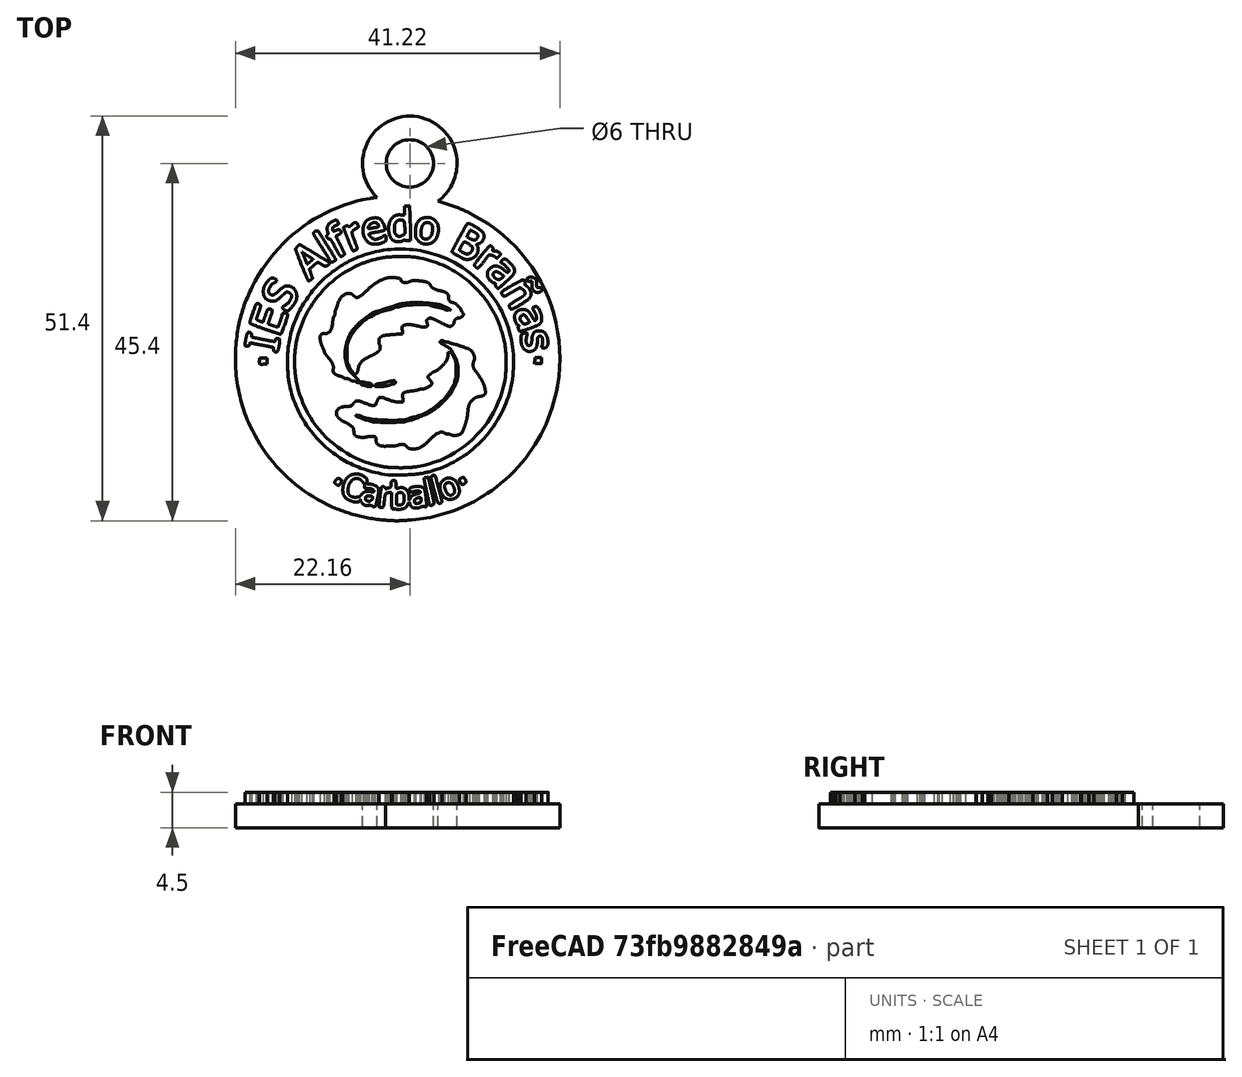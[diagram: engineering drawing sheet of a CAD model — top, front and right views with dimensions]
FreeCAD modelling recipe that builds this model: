
FCSTD DOCUMENT  (FreeCAD 0.18R16093 +53 (Git))
Label: Chaveiro_IES_AlfredoBranas
License: All rights reserved
LicenseURL: http://en.wikipedia.org/wiki/All_rights_reserved
objects: Part::Feature×90, Part::Extrusion×49, Part::Cut×15, Part::MultiFuse×3, Part::Cylinder×2
note: 159 computed .brp shape members not serialized (recipe doc carries the construction recipe); baked Part::Feature solids carry a one-line shape summary decoded from their .brp

FEATURE [Part::Feature] path55
  shape: bbox 42.61 x 41.74 x 2e-07 mm, 1 faces, 0 solids (baked)
FEATURE [Part::Feature] path55002
  shape: bbox 6.061 x 3.668 x 2e-07 mm, 1 faces, 0 solids (baked)
FEATURE [Part::Feature] path55003
  shape: bbox 3.579 x 3.321 x 2e-07 mm, 1 faces, 0 solids (baked)
FEATURE [Part::Feature] path55004
  shape: bbox 1.385 x 2.117 x 2e-07 mm, 1 faces, 0 solids (baked)
FEATURE [Part::Feature] path55005
  shape: bbox 1.072 x 1.725 x 2e-07 mm, 1 faces, 0 solids (baked)
FEATURE [Part::Feature] path55006
  shape: bbox 1.986 x 2.775 x 2e-07 mm, 1 faces, 0 solids (baked)
FEATURE [Part::Feature] path55007
  shape: bbox 1.276 x 1.287 x 2e-07 mm, 1 faces, 0 solids (baked)
FEATURE [Part::Feature] path55008
  shape: bbox 0.8533 x 0.8673 x 2e-07 mm, 1 faces, 0 solids (baked)
FEATURE [Part::Feature] path55009
  shape: bbox 4.663 x 4.271 x 2e-07 mm, 1 faces, 0 solids (baked)
FEATURE [Part::Feature] path55010
  shape: bbox 2.231 x 2.679 x 2e-07 mm, 1 faces, 0 solids (baked)
FEATURE [Part::Feature] path55011
  shape: bbox 1.459 x 1.242 x 2e-07 mm, 1 faces, 0 solids (baked)
FEATURE [Part::Feature] path55012
  shape: bbox 1.04 x 0.7778 x 2e-07 mm, 1 faces, 0 solids (baked)
FEATURE [Part::Feature] path55013
  shape: bbox 3.128 x 3.518 x 2e-07 mm, 1 faces, 0 solids (baked)
FEATURE [Part::Feature] path55014
  shape: bbox 3.478 x 2.454 x 2e-07 mm, 1 faces, 0 solids (baked)
FEATURE [Part::Feature] path55015
  shape: bbox 1.292 x 3.612 x 2e-07 mm, 1 faces, 0 solids (baked)
FEATURE [Part::Feature] path55016
  shape: bbox 0.9434 x 3.157 x 2e-07 mm, 1 faces, 0 solids (baked)
FEATURE [Part::Feature] path55017
  shape: bbox 1.497 x 3.752 x 2e-07 mm, 1 faces, 0 solids (baked)
FEATURE [Part::Feature] path55018
  shape: bbox 1.034 x 3.318 x 2e-07 mm, 1 faces, 0 solids (baked)
FEATURE [Part::Feature] path55019
  shape: bbox 2.911 x 2.992 x 2e-07 mm, 1 faces, 0 solids (baked)
FEATURE [Part::Feature] path55020
  shape: bbox 2.421 x 2.668 x 2e-07 mm, 1 faces, 0 solids (baked)
FEATURE [Part::Feature] path55021
  shape: bbox 1.627 x 2.283 x 2e-07 mm, 1 faces, 0 solids (baked)
FEATURE [Part::Feature] path55022
  shape: bbox 1.515 x 1.829 x 2e-07 mm, 1 faces, 0 solids (baked)
FEATURE [Part::Feature] path55023
  shape: bbox 0.9527 x 1.028 x 2e-07 mm, 1 faces, 0 solids (baked)
FEATURE [Part::Feature] path55024
  shape: bbox 0.4535 x 0.6054 x 2e-07 mm, 1 faces, 0 solids (baked)
FEATURE [Part::Feature] path55025
  shape: bbox 0.9424 x 1.049 x 2e-07 mm, 1 faces, 0 solids (baked)
FEATURE [Part::Feature] path55026
  shape: bbox 0.4617 x 0.5401 x 2e-07 mm, 1 faces, 0 solids (baked)
FEATURE [Part::Feature] path55027
  shape: bbox 29.22 x 29.06 x 2e-07 mm, 1 faces, 0 solids (baked)
FEATURE [Part::Feature] path55028
  shape: bbox 29.61 x 29.75 x 2e-07 mm, 1 faces, 0 solids (baked)
FEATURE [Part::Feature] path55029
  shape: bbox 27.42 x 27.59 x 2e-07 mm, 1 faces, 0 solids (baked)
FEATURE [Part::Feature] path55030
  shape: bbox 27.03 x 26.91 x 2e-07 mm, 1 faces, 0 solids (baked)
FEATURE [Part::Feature] path55031
  shape: bbox 18.97 x 13.82 x 2e-07 mm, 1 faces, 0 solids (baked)
FEATURE [Part::Feature] path55032
  shape: bbox 18.57 x 13.17 x 2e-07 mm, 1 faces, 0 solids (baked)
FEATURE [Part::Feature] path55033
  shape: bbox 1.628 x 0.6369 x 2e-07 mm, 1 faces, 0 solids (baked)
FEATURE [Part::Feature] path55034
  shape: bbox 2.68 x 0.7825 x 2e-07 mm, 1 faces, 0 solids (baked)
FEATURE [Part::Feature] path55035
  shape: bbox 18.3 x 13.46 x 2e-07 mm, 1 faces, 0 solids (baked)
FEATURE [Part::Feature] path55036
  shape: bbox 17.74 x 12.84 x 2e-07 mm, 1 faces, 0 solids (baked)
FEATURE [Part::Feature] path55037
  shape: bbox 0.9811 x 0.8129 x 2e-07 mm, 1 faces, 0 solids (baked)
FEATURE [Part::Feature] path55038
  shape: bbox 0.7466 x 0.567 x 2e-07 mm, 1 faces, 0 solids (baked)
FEATURE [Part::Feature] path55039
  shape: bbox 0.9057 x 0.8199 x 2e-07 mm, 1 faces, 0 solids (baked)
FEATURE [Part::Feature] path55040
  shape: bbox 0.5973 x 0.512 x 2e-07 mm, 1 faces, 0 solids (baked)
FEATURE [Part::Feature] path55041
  shape: bbox 4.394 x 2.557 x 2e-07 mm, 1 faces, 0 solids (baked)
FEATURE [Part::Feature] path55042
  shape: bbox 4.112 x 2.264 x 2e-07 mm, 1 faces, 0 solids (baked)
FEATURE [Part::Feature] path55043
  shape: bbox 3.481 x 2.717 x 2e-07 mm, 1 faces, 0 solids (baked)
FEATURE [Part::Feature] path55044
  shape: bbox 3.298 x 2.6 x 2e-07 mm, 1 faces, 0 solids (baked)
FEATURE [Part::Feature] path55045
  shape: bbox 4.911 x 3.979 x 2e-07 mm, 1 faces, 0 solids (baked)
FEATURE [Part::Feature] path55046
  shape: bbox 4.39 x 3.462 x 2e-07 mm, 1 faces, 0 solids (baked)
FEATURE [Part::Feature] path55047
  shape: bbox 3.605 x 3.157 x 2e-07 mm, 1 faces, 0 solids (baked)
FEATURE [Part::Feature] path55048
  shape: bbox 3.359 x 2.795 x 2e-07 mm, 1 faces, 0 solids (baked)
FEATURE [Part::Feature] path55049
  shape: bbox 1.712 x 1.573 x 2e-07 mm, 1 faces, 0 solids (baked)
FEATURE [Part::Feature] path55050
  shape: bbox 1.261 x 1.265 x 2e-07 mm, 1 faces, 0 solids (baked)
FEATURE [Part::Feature] path55051
  shape: bbox 4.529 x 4.348 x 2e-07 mm, 1 faces, 0 solids (baked)
FEATURE [Part::Feature] path55052
  shape: bbox 4.156 x 3.945 x 2e-07 mm, 1 faces, 0 solids (baked)
FEATURE [Part::Feature] path55053
  shape: bbox 3.991 x 3.755 x 2e-07 mm, 1 faces, 0 solids (baked)
FEATURE [Part::Feature] path55054
  shape: bbox 3.399 x 3.294 x 2e-07 mm, 1 faces, 0 solids (baked)
FEATURE [Part::Feature] path55055
  shape: bbox 2.278 x 2.07 x 2e-07 mm, 1 faces, 0 solids (baked)
FEATURE [Part::Feature] path55056
  shape: bbox 1.608 x 1.762 x 2e-07 mm, 1 faces, 0 solids (baked)
FEATURE [Part::Feature] path55057
  shape: bbox 3.883 x 3.859 x 2e-07 mm, 1 faces, 0 solids (baked)
FEATURE [Part::Feature] path55058
  shape: bbox 3.461 x 3.318 x 2e-07 mm, 1 faces, 0 solids (baked)
FEATURE [Part::Feature] path55059
  shape: bbox 1.711 x 1.509 x 2e-07 mm, 1 faces, 0 solids (baked)
FEATURE [Part::Feature] path55060
  shape: bbox 1.522 x 1.079 x 2e-07 mm, 1 faces, 0 solids (baked)
FEATURE [Part::Feature] path55061
  shape: bbox 4.369 x 4.646 x 2e-07 mm, 1 faces, 0 solids (baked)
FEATURE [Part::Feature] path55062
  shape: bbox 3.885 x 4.096 x 2e-07 mm, 1 faces, 0 solids (baked)
FEATURE [Part::Feature] path55063
  shape: bbox 1.848 x 2.086 x 2e-07 mm, 1 faces, 0 solids (baked)
FEATURE [Part::Feature] path55064
  shape: bbox 1.372 x 1.537 x 2e-07 mm, 1 faces, 0 solids (baked)
FEATURE [Part::Feature] path55065
  shape: bbox 3.325 x 2.896 x 2e-07 mm, 1 faces, 0 solids (baked)
FEATURE [Part::Feature] path55066
  shape: bbox 2.837 x 2.413 x 2e-07 mm, 1 faces, 0 solids (baked)
FEATURE [Part::Feature] path55067
  shape: bbox 2.873 x 4.076 x 2e-07 mm, 1 faces, 0 solids (baked)
FEATURE [Part::Feature] path55068
  shape: bbox 2.418 x 3.68 x 2e-07 mm, 1 faces, 0 solids (baked)
FEATURE [Part::Feature] path55069
  shape: bbox 4.187 x 4.703 x 2e-07 mm, 1 faces, 0 solids (baked)
FEATURE [Part::Feature] path55070
  shape: bbox 3.672 x 4.259 x 2e-07 mm, 1 faces, 0 solids (baked)
FEATURE [Part::Feature] path55071
  shape: bbox 2.278 x 1.964 x 2e-07 mm, 1 faces, 0 solids (baked)
FEATURE [Part::Feature] path55072
  shape: bbox 1.728 x 1.688 x 2e-07 mm, 1 faces, 0 solids (baked)
FEATURE [Part::Feature] path55073
  shape: bbox 2.013 x 1.62 x 2e-07 mm, 1 faces, 0 solids (baked)
FEATURE [Part::Feature] path55074
  shape: bbox 1.478 x 1.273 x 2e-07 mm, 1 faces, 0 solids (baked)
FEATURE [Part::Feature] path55075
  shape: bbox 2.371 x 4.711 x 2e-07 mm, 1 faces, 0 solids (baked)
FEATURE [Part::Feature] path55076
  shape: bbox 1.938 x 4.293 x 2e-07 mm, 1 faces, 0 solids (baked)
FEATURE [Part::Feature] path55077
  shape: bbox 1.959 x 3.712 x 2e-07 mm, 1 faces, 0 solids (baked)
FEATURE [Part::Feature] path55078
  shape: bbox 1.513 x 3.257 x 2e-07 mm, 1 faces, 0 solids (baked)
FEATURE [Part::Feature] path55079
  shape: bbox 3.202 x 3.458 x 2e-07 mm, 1 faces, 0 solids (baked)
FEATURE [Part::Feature] path55080
  shape: bbox 2.817 x 3.087 x 2e-07 mm, 1 faces, 0 solids (baked)
FEATURE [Part::Feature] path55081
  shape: bbox 1.855 x 1.145 x 2e-07 mm, 1 faces, 0 solids (baked)
FEATURE [Part::Feature] path55082
  shape: bbox 1.522 x 0.9057 x 2e-07 mm, 1 faces, 0 solids (baked)
FEATURE [Part::Feature] path55083
  shape: bbox 3.154 x 3.493 x 2e-07 mm, 1 faces, 0 solids (baked)
FEATURE [Part::Feature] path55084
  shape: bbox 2.742 x 3.32 x 2e-07 mm, 1 faces, 0 solids (baked)
FEATURE [Part::Feature] path55085
  shape: bbox 1.893 x 2.907 x 2e-07 mm, 1 faces, 0 solids (baked)
FEATURE [Part::Feature] path55086
  shape: bbox 1.599 x 2.338 x 2e-07 mm, 1 faces, 0 solids (baked)
FEATURE [Part::Feature] path55087
  shape: bbox 2.901 x 4.614 x 2e-07 mm, 1 faces, 0 solids (baked)
FEATURE [Part::Feature] path55088
  shape: bbox 2.574 x 4.276 x 2e-07 mm, 1 faces, 0 solids (baked)
FEATURE [Part::Feature] path55089
  shape: bbox 1.694 x 2.496 x 2e-07 mm, 1 faces, 0 solids (baked)
FEATURE [Part::Feature] path55090
  shape: bbox 1.455 x 2.377 x 2e-07 mm, 1 faces, 0 solids (baked)
FEATURE [Part::Extrusion] Extrude
  Base = -> path55002
  Dir = (0,0,1)
  DirMode = 0
  FaceMakerClass = Part::FaceMakerBullseye
  LengthFwd = 1.5
  LengthRev = 0
  Solid = true
  Symmetric = false
FEATURE [Part::Extrusion] Extrude003
  Base = -> path55005
  Dir = (0,0,1)
  DirMode = 0
  FaceMakerClass = Part::FaceMakerBullseye
  LengthFwd = 1.5
  LengthRev = 0
  Solid = true
  Symmetric = false
FEATURE [Part::Extrusion] Extrude006
  Base = -> path55008
  Dir = (0,0,1)
  DirMode = 0
  FaceMakerClass = Part::FaceMakerBullseye
  LengthFwd = 1.5
  LengthRev = 0
  Solid = true
  Symmetric = false
FEATURE [Part::Extrusion] Extrude007
  Base = -> path55009
  Dir = (0,0,1)
  DirMode = 0
  FaceMakerClass = Part::FaceMakerBullseye
  LengthFwd = 1.5
  LengthRev = 0
  Solid = true
  Symmetric = false
FEATURE [Part::Extrusion] Extrude010
  Base = -> path55012
  Dir = (0,0,1)
  DirMode = 0
  FaceMakerClass = Part::FaceMakerBullseye
  LengthFwd = 7.5
  LengthRev = 0
  Placement = pos=(0,0,-2) rot=(0,0,1;0rad)
  Solid = true
  Symmetric = false
FEATURE [Part::Extrusion] Extrude012
  Base = -> path55014
  Dir = (0,0,1)
  DirMode = 0
  FaceMakerClass = Part::FaceMakerBullseye
  LengthFwd = 1.5
  LengthRev = 0
  Solid = true
  Symmetric = false
FEATURE [Part::Extrusion] Extrude013
  Base = -> path55015
  Dir = (0,0,1)
  DirMode = 0
  FaceMakerClass = Part::FaceMakerBullseye
  LengthFwd = 1.5
  LengthRev = 0
  Solid = true
  Symmetric = false
FEATURE [Part::Extrusion] Extrude015
  Base = -> path55017
  Dir = (0,0,1)
  DirMode = 0
  FaceMakerClass = Part::FaceMakerBullseye
  LengthFwd = 1.5
  LengthRev = 0
  Solid = true
  Symmetric = false
FEATURE [Part::Extrusion] Extrude017
  Base = -> path55019
  Dir = (0,0,1)
  DirMode = 0
  FaceMakerClass = Part::FaceMakerBullseye
  LengthFwd = 1.5
  LengthRev = 0
  Solid = true
  Symmetric = false
FEATURE [Part::Extrusion] Extrude020
  Base = -> path55022
  Dir = (0,0,1)
  DirMode = 0
  FaceMakerClass = Part::FaceMakerBullseye
  LengthFwd = 1.5
  LengthRev = 0
  Solid = true
  Symmetric = false
FEATURE [Part::Extrusion] Extrude021
  Base = -> path55023
  Dir = (0,0,1)
  DirMode = 0
  FaceMakerClass = Part::FaceMakerBullseye
  LengthFwd = 1.5
  LengthRev = 0
  Solid = true
  Symmetric = false
FEATURE [Part::Extrusion] Extrude022
  Base = -> path55024
  Dir = (0,0,1)
  DirMode = 0
  FaceMakerClass = Part::FaceMakerBullseye
  LengthFwd = 1.5
  LengthRev = 0
  Solid = true
  Symmetric = false
FEATURE [Part::Extrusion] Extrude023
  Base = -> path55025
  Dir = (0,0,1)
  DirMode = 0
  FaceMakerClass = Part::FaceMakerBullseye
  LengthFwd = 1.5
  LengthRev = 0
  Solid = true
  Symmetric = false
FEATURE [Part::Extrusion] Extrude025
  Base = -> path55027
  Dir = (0,0,1)
  DirMode = 0
  FaceMakerClass = Part::FaceMakerBullseye
  LengthFwd = 1.5
  LengthRev = 0
  Solid = true
  Symmetric = false
FEATURE [Part::Extrusion] Extrude028
  Base = -> path55030
  Dir = (0,0,1)
  DirMode = 0
  FaceMakerClass = Part::FaceMakerBullseye
  LengthFwd = 1.5
  LengthRev = 0
  Solid = true
  Symmetric = false
FEATURE [Part::Extrusion] Extrude029
  Base = -> path55031
  Dir = (0,0,1)
  DirMode = 0
  FaceMakerClass = Part::FaceMakerBullseye
  LengthFwd = 1.5
  LengthRev = 0
  Solid = true
  Symmetric = false
FEATURE [Part::Extrusion] Extrude030
  Base = -> path55032
  Dir = (0,0,1)
  DirMode = 0
  FaceMakerClass = Part::FaceMakerBullseye
  LengthFwd = 1.5
  LengthRev = 0
  Solid = true
  Symmetric = false
FEATURE [Part::Extrusion] Extrude031
  Base = -> path55033
  Dir = (0,0,1)
  DirMode = 0
  FaceMakerClass = Part::FaceMakerBullseye
  LengthFwd = 1.5
  LengthRev = 0
  Solid = true
  Symmetric = false
FEATURE [Part::Extrusion] Extrude032
  Base = -> path55034
  Dir = (0,0,1)
  DirMode = 0
  FaceMakerClass = Part::FaceMakerBullseye
  LengthFwd = 1.5
  LengthRev = 0
  Solid = true
  Symmetric = false
FEATURE [Part::Extrusion] Extrude033
  Base = -> path55035
  Dir = (0,0,1)
  DirMode = 0
  FaceMakerClass = Part::FaceMakerBullseye
  LengthFwd = 1.5
  LengthRev = 0
  Solid = true
  Symmetric = false
FEATURE [Part::Extrusion] Extrude034
  Base = -> path55036
  Dir = (0,0,1)
  DirMode = 0
  FaceMakerClass = Part::FaceMakerBullseye
  LengthFwd = 1.5
  LengthRev = 0
  Solid = true
  Symmetric = false
FEATURE [Part::Extrusion] Extrude035
  Base = -> path55037
  Dir = (0,0,1)
  DirMode = 0
  FaceMakerClass = Part::FaceMakerBullseye
  LengthFwd = 1.5
  LengthRev = 0
  Solid = true
  Symmetric = false
FEATURE [Part::Extrusion] Extrude037
  Base = -> path55039
  Dir = (0,0,1)
  DirMode = 0
  FaceMakerClass = Part::FaceMakerBullseye
  LengthFwd = 1.5
  LengthRev = 0
  Solid = true
  Symmetric = false
FEATURE [Part::Extrusion] Extrude039
  Base = -> path55041
  Dir = (0,0,1)
  DirMode = 0
  FaceMakerClass = Part::FaceMakerBullseye
  LengthFwd = 1.5
  LengthRev = 0
  Solid = true
  Symmetric = false
FEATURE [Part::Extrusion] Extrude041
  Base = -> path55043
  Dir = (0,0,1)
  DirMode = 0
  FaceMakerClass = Part::FaceMakerBullseye
  LengthFwd = 1.5
  LengthRev = 0
  Solid = true
  Symmetric = false
FEATURE [Part::Extrusion] Extrude043
  Base = -> path55045
  Dir = (0,0,1)
  DirMode = 0
  FaceMakerClass = Part::FaceMakerBullseye
  LengthFwd = 1.5
  LengthRev = 0
  Solid = true
  Symmetric = false
FEATURE [Part::Extrusion] Extrude045
  Base = -> path55047
  Dir = (0,0,1)
  DirMode = 0
  FaceMakerClass = Part::FaceMakerBullseye
  LengthFwd = 1.5
  LengthRev = 0
  Solid = true
  Symmetric = false
FEATURE [Part::Extrusion] Extrude048
  Base = -> path55050
  Dir = (0,0,1)
  DirMode = 0
  FaceMakerClass = Part::FaceMakerBullseye
  LengthFwd = 1.5
  LengthRev = 0
  Solid = true
  Symmetric = false
FEATURE [Part::Extrusion] Extrude049
  Base = -> path55051
  Dir = (0,0,1)
  DirMode = 0
  FaceMakerClass = Part::FaceMakerBullseye
  LengthFwd = 1.5
  LengthRev = 0
  Solid = true
  Symmetric = false
FEATURE [Part::Extrusion] Extrude051
  Base = -> path55053
  Dir = (0,0,1)
  DirMode = 0
  FaceMakerClass = Part::FaceMakerBullseye
  LengthFwd = 1.5
  LengthRev = 0
  Solid = true
  Symmetric = false
FEATURE [Part::Extrusion] Extrude053
  Base = -> path55055
  Dir = (0,0,1)
  DirMode = 0
  FaceMakerClass = Part::FaceMakerBullseye
  LengthFwd = 1.5
  LengthRev = 0
  Solid = true
  Symmetric = false
FEATURE [Part::Extrusion] Extrude055
  Base = -> path55057
  Dir = (0,0,1)
  DirMode = 0
  FaceMakerClass = Part::FaceMakerBullseye
  LengthFwd = 1.5
  LengthRev = 0
  Solid = true
  Symmetric = false
FEATURE [Part::Extrusion] Extrude058
  Base = -> path55060
  Dir = (0,0,1)
  DirMode = 0
  FaceMakerClass = Part::FaceMakerBullseye
  LengthFwd = 1.5
  LengthRev = 0
  Solid = true
  Symmetric = false
FEATURE [Part::Extrusion] Extrude059
  Base = -> path55061
  Dir = (0,0,1)
  DirMode = 0
  FaceMakerClass = Part::FaceMakerBullseye
  LengthFwd = 1.5
  LengthRev = 0
  Solid = true
  Symmetric = false
FEATURE [Part::Extrusion] Extrude062
  Base = -> path55064
  Dir = (0,0,1)
  DirMode = 0
  FaceMakerClass = Part::FaceMakerBullseye
  LengthFwd = 1.5
  LengthRev = 0
  Solid = true
  Symmetric = false
FEATURE [Part::Extrusion] Extrude063
  Base = -> path55065
  Dir = (0,0,1)
  DirMode = 0
  FaceMakerClass = Part::FaceMakerBullseye
  LengthFwd = 1.5
  LengthRev = 0
  Solid = true
  Symmetric = false
FEATURE [Part::Extrusion] Extrude065
  Base = -> path55067
  Dir = (0,0,1)
  DirMode = 0
  FaceMakerClass = Part::FaceMakerBullseye
  LengthFwd = 1.5
  LengthRev = 0
  Solid = true
  Symmetric = false
FEATURE [Part::Extrusion] Extrude067
  Base = -> path55069
  Dir = (0,0,1)
  DirMode = 0
  FaceMakerClass = Part::FaceMakerBullseye
  LengthFwd = 1.5
  LengthRev = 0
  Solid = true
  Symmetric = false
FEATURE [Part::Extrusion] Extrude070
  Base = -> path55072
  Dir = (0,0,1)
  DirMode = 0
  FaceMakerClass = Part::FaceMakerBullseye
  LengthFwd = 1.5
  LengthRev = 0
  Solid = true
  Symmetric = false
FEATURE [Part::Extrusion] Extrude072
  Base = -> path55074
  Dir = (0,0,1)
  DirMode = 0
  FaceMakerClass = Part::FaceMakerBullseye
  LengthFwd = 1.5
  LengthRev = 0
  Solid = true
  Symmetric = false
FEATURE [Part::Extrusion] Extrude073
  Base = -> path55075
  Dir = (0,0,1)
  DirMode = 0
  FaceMakerClass = Part::FaceMakerBullseye
  LengthFwd = 1.5
  LengthRev = 0
  Solid = true
  Symmetric = false
FEATURE [Part::Extrusion] Extrude075
  Base = -> path55077
  Dir = (0,0,1)
  DirMode = 0
  FaceMakerClass = Part::FaceMakerBullseye
  LengthFwd = 1.5
  LengthRev = 0
  Solid = true
  Symmetric = false
FEATURE [Part::Extrusion] Extrude077
  Base = -> path55079
  Dir = (0,0,1)
  DirMode = 0
  FaceMakerClass = Part::FaceMakerBullseye
  LengthFwd = 1.5
  LengthRev = 0
  Solid = true
  Symmetric = false
FEATURE [Part::Extrusion] Extrude080
  Base = -> path55082
  Dir = (0,0,1)
  DirMode = 0
  FaceMakerClass = Part::FaceMakerBullseye
  LengthFwd = 1.5
  LengthRev = 0
  Solid = true
  Symmetric = false
FEATURE [Part::Extrusion] Extrude081
  Base = -> path55083
  Dir = (0,0,1)
  DirMode = 0
  FaceMakerClass = Part::FaceMakerBullseye
  LengthFwd = 1.5
  LengthRev = 0
  Solid = true
  Symmetric = false
FEATURE [Part::Extrusion] Extrude084
  Base = -> path55086
  Dir = (0,0,1)
  DirMode = 0
  FaceMakerClass = Part::FaceMakerBullseye
  LengthFwd = 1.5
  LengthRev = 0
  Solid = true
  Symmetric = false
FEATURE [Part::Extrusion] Extrude085
  Base = -> path55087
  Dir = (0,0,1)
  DirMode = 0
  FaceMakerClass = Part::FaceMakerBullseye
  LengthFwd = 1.5
  LengthRev = 0
  Solid = true
  Symmetric = false
FEATURE [Part::Extrusion] Extrude088
  Base = -> path55090
  Dir = (0,0,1)
  DirMode = 0
  FaceMakerClass = Part::FaceMakerBullseye
  LengthFwd = 1.5
  LengthRev = 0
  Solid = true
  Symmetric = false
FEATURE [Part::Cut] Cut001
  Base = -> Extrude
  Tool = -> Extrude003
FEATURE [Part::Cut] Cut002
  Base = -> Extrude017
  Tool = -> Extrude020
FEATURE [Part::Cut] Cut003
  Base = -> Extrude007
  Tool = -> Extrude012
FEATURE [Part::Cut] Cut004
  Base = -> Extrude045
  Tool = -> Extrude048
FEATURE [Part::Cut] Cut005
  Base = -> Extrude055
  Tool = -> Extrude058
FEATURE [Part::Cut] Cut006
  Base = -> Extrude059
  Tool = -> Extrude062
FEATURE [Part::Cut] Cut007
  Base = -> Extrude067
  Tool = -> Extrude070
FEATURE [Part::Cut] Cut008
  Base = -> Extrude077
  Tool = -> Extrude080
FEATURE [Part::Cut] Cut009
  Base = -> Extrude081
  Tool = -> Extrude084
FEATURE [Part::Cut] Cut010
  Base = -> Extrude085
  Tool = -> Extrude088
FEATURE [Part::Cut] Cut011
  Base = -> Cut007
  Tool = -> Extrude072
FEATURE [Part::Cut] Cut012
  Base = -> Cut001
  Tool = -> Extrude006
FEATURE [Part::Cut] Cut
  Base = -> Cut003
  Tool = -> Extrude010
FEATURE [Part::Cut] Cut013
  Base = -> Extrude025
  Tool = -> Extrude028
FEATURE [Part::Extrusion] Extrude089
  Base = -> path55
  Dir = (0,0,-1)
  DirMode = 0
  FaceMakerClass = Part::FaceMakerBullseye
  LengthFwd = 3
  LengthRev = 0
  Solid = true
  Symmetric = false
FEATURE [Part::Cylinder] Cylinder
  Angle = 360
  AttacherType = Attacher::AttachEngine3D
  Height = 3
  Radius = 6
FEATURE [Part::Cylinder] Cylinder001
  Angle = 360
  AttacherType = Attacher::AttachEngine3D
  Height = 3
  Radius = 3
FEATURE [Part::Cut] Cut014
  Base = -> Cylinder
  Placement = pos=(44,-14,-3) rot=(0,0,1;0rad)
  Tool = -> Cylinder001
FEATURE [Part::MultiFuse] Fusion
  Shapes = -> [Extrude013,Extrude015,Extrude021,Extrude023,Extrude022,Extrude029,Extrude031,Extrude030,Extrude032,Extrude033,Extrude035,Extrude034,Extrude037,Extrude039,Extrude043,Extrude041,Extrude049,Extrude051,Extrude053,Extrude063,Extrude065,Extrude073,Extrude075]
FEATURE [Part::MultiFuse] Fusion001
  Shapes = -> [Cut002,Cut004,Cut006,Cut005,Cut008,Cut010,Cut009,Cut011,Cut012,Cut,Cut013]
FEATURE [Part::MultiFuse] Fusion002  label="Chaveiro"
  Shapes = -> [Extrude089,Cut014,Fusion,Fusion001]
